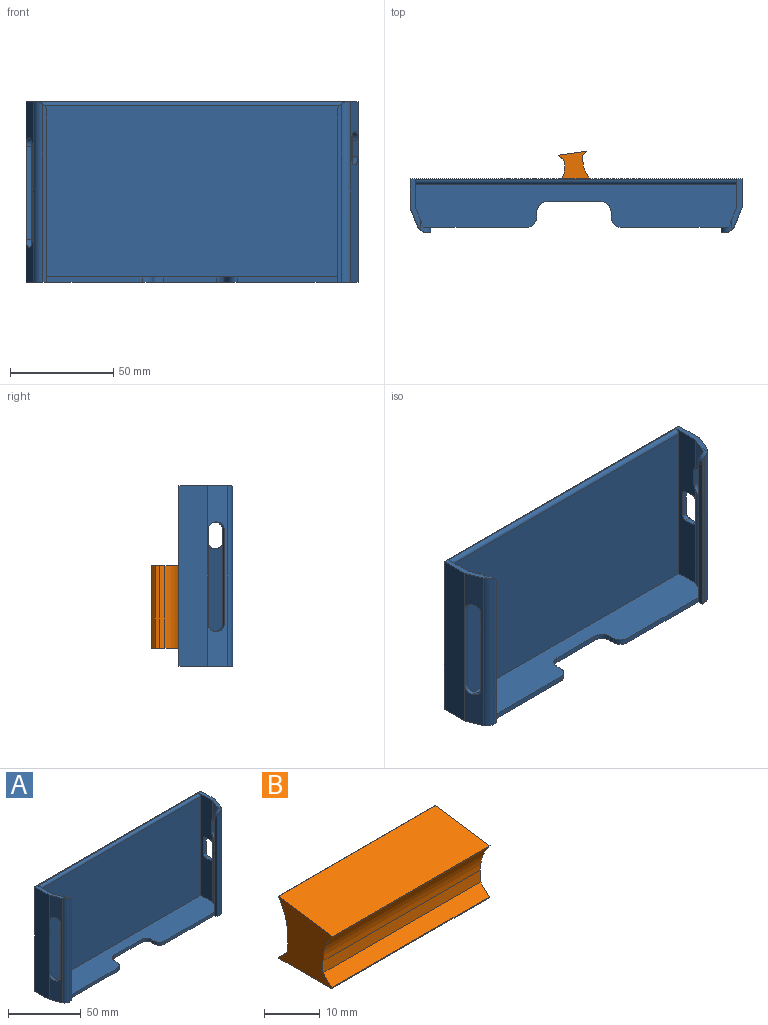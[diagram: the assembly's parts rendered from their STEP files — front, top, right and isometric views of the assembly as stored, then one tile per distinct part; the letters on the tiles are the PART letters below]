
ASSEMBLY  parts=2 mates=1
PART A: 57 faces, bbox 161x26x87.6 mm
  f0: plane 48.4x2.6mm, normal (0,-1,0), area 125.8mm2, adj f2,f3,f42,f48
  f1: plane 46.4x2.6mm, normal (0,-1,0), area 120.6mm2, adj f2,f3,f43,f52
  f2: plane 161x26mm, normal (0,0,-1), area 3307.5mm2, adj f0,f1,f6,f9,f10,f13,f14,f27
  f3: plane 155.8x20.8mm, normal (0,0,1), area 2754.5mm2, adj f0,f1,f4,f5,f8,f11,f12,f27
  f4: plane 85x13.3mm, normal (-1,0,0), area 803.1mm2, adj f3,f5,f7,f8,f15,f16,f17,f19
  f5: plane 85.03x9.53mm, normal (-0.93,0.37,0), area 750.4mm2, adj f3,f4,f7,f18,f20,f21,f22,f34
  f6: plane 87.6x9.5mm, normal (0.93,-0.37,0), area 766mm2, adj f2,f7,f14,f18,f20,f21,f22,f34
  f7: plane 161x24.93mm, normal (0,0,1), area 213.2mm2, adj f4,f5,f6,f9,f10,f11,f12,f13
  f8: plane 155.8x83mm, normal (0,-1,0), area 12931.4mm2, adj f3,f4,f12,f46
  f9: plane 161x87.6mm, normal (0,1,0), area 14103.6mm2, adj f2,f7,f13,f14
  f10: plane 87.6x9.5mm, normal (-0.93,-0.37,0), area 458.7mm2, adj f2,f7,f13,f23,f24,f25,f26,f30
  f11: plane 85.03x9.53mm, normal (0.93,0.37,0), area 467.3mm2, adj f3,f7,f12,f23,f24,f26,f30,f31
  f12: plane 85x13.3mm, normal (1,0,0), area 923.2mm2, adj f3,f7,f8,f11,f25,f31,f32,f46
  f13: plane 87.6x13.9mm, normal (-1,0,0), area 1217.6mm2, adj f2,f7,f9,f10
  f14: plane 87.6x13.9mm, normal (1,0,0), area 1071.4mm2, adj f2,f6,f7,f9,f15,f16,f17,f19
  f15: plane 4.7x2.6mm, normal (0,0,1), area 12.2mm2, adj f4,f14,f38,f39
  f16: plane 4.7x2.6mm, normal (0,0,-1), area 12.2mm2, adj f4,f14,f40,f41
  f17: plane 13.2x2.6mm, normal (0,-1,0), area 34.3mm2, adj f4,f14,f39,f40
  f18: plane 13.2x2.6mm, normal (0,1,0), area 34.3mm2, adj f5,f6,f38,f41
  f19: plane 8x2.6mm, normal (-0.37,-0.93,0), area 22.4mm2, adj f4,f14,f34,f35
  f20: plane 2.61x1.83mm, normal (0,0,1), area 2.4mm2, adj f5,f6,f34,f37
  f21: plane 2.61x1.83mm, normal (0,0,-1), area 2.4mm2, adj f5,f6,f35,f36
  f22: plane 8x2.24mm, normal (0.37,0.93,0), area 19.3mm2, adj f5,f6,f36,f37
  f23: plane 45.1x2.24mm, normal (-0.37,0.93,0), area 108.9mm2, adj f10,f11,f30,f33
  f24: plane 2.43x1.36mm, normal (0,0,-1), area 1.2mm2, adj f10,f11,f30,f31
  f25: plane 45.1x2.51mm, normal (0.37,-0.93,0), area 122.1mm2, adj f10,f12,f31,f32
  f26: plane 2.43x1.36mm, normal (0,0,1), area 1.2mm2, adj f10,f11,f32,f33
  f27: plane 2.6x2.5mm, normal (-1,0,0), area 6.5mm2, adj f2,f3,f42,f45
  f28: plane 2.6x2.5mm, normal (1,0,0), area 6.5mm2, adj f2,f3,f43,f44
  f29: plane 26x2.6mm, normal (0,-1,0), area 67.6mm2, adj f2,f3,f44,f45
  f30: cylinder r=4mm len=4.61mm, axis (0.93,0.37,0), area 15.2mm2, adj f10,f11,f23,f24
  f31: cylinder r=4mm len=4.72mm, axis (-0.93,-0.37,0), area 15.6mm2, adj f10,f11,f12,f24,f25
  f32: cylinder r=4mm len=4.72mm, axis (0.93,0.37,0), area 15.6mm2, adj f10,f11,f12,f25,f26
  f33: cylinder r=4mm len=4.61mm, axis (-0.93,-0.37,0), area 15.2mm2, adj f10,f11,f23,f26
  f34: cylinder r=4mm len=4.75mm, axis (0.93,-0.37,0), area 15.9mm2, adj f4,f5,f6,f19,f20
  f35: cylinder r=4mm len=4.75mm, axis (-0.93,0.37,0), area 15.9mm2, adj f4,f5,f6,f19,f21
  f36: cylinder r=4mm len=4.61mm, axis (-0.93,0.37,0), area 15.2mm2, adj f5,f6,f21,f22
  f37: cylinder r=4mm len=4.61mm, axis (0.93,-0.37,0), area 15.2mm2, adj f5,f6,f20,f22
  f38: cylinder r=2mm len=2.6mm, axis (1,0,0), area 8.2mm2, adj f4,f14,f15,f18
  f39: cylinder r=2mm len=2.6mm, axis (1,0,0), area 8.2mm2, adj f4,f14,f15,f17
  f40: cylinder r=2mm len=2.6mm, axis (-1,0,0), area 8.2mm2, adj f4,f14,f16,f17
  f41: cylinder r=2mm len=2.6mm, axis (-1,0,0), area 8.2mm2, adj f4,f14,f16,f18
  f42: cylinder r=5mm len=5mm, axis (0,0,1), area 20.4mm2, adj f0,f2,f3,f27
  f43: cylinder r=5mm len=5mm, axis (0,0,-1), area 20.4mm2, adj f1,f2,f3,f28
  f44: cylinder r=5mm len=5mm, axis (0,0,1), area 20.4mm2, adj f2,f3,f28,f29
  f45: cylinder r=5mm len=5mm, axis (0,0,-1), area 20.4mm2, adj f2,f3,f27,f29
  f46: cylinder r=2mm len=155.8mm, axis (1,0,0), area 489.5mm2, adj f4,f7,f8,f12
  f47: plane 84.83x3.7mm, normal (0,1,0), area 309.2mm2, adj f3,f5,f48,f50
  f48: plane 82.6x2.6mm, normal (-1,0,0), area 214.8mm2, adj f0,f2,f47,f49,f50
  f49: plane 86.53x1.91mm, normal (0,-1,0), area 163.3mm2, adj f2,f48,f50,f51
  f50: cylinder r=5mm len=5.85mm, axis (0,-1,0), area 21.5mm2, adj f5,f7,f47,f48,f49,f51
  f51: cylinder r=5mm len=87.6mm, axis (0,0,-1), area 467.7mm2, adj f2,f6,f7,f49,f50
  f52: plane 82.6x2.6mm, normal (1,0,0), area 214.8mm2, adj f1,f2,f53,f54,f55
  f53: plane 86.53x1.91mm, normal (0,-1,0), area 163.3mm2, adj f2,f52,f55,f56
  f54: plane 84.83x3.7mm, normal (0,1,0), area 309.2mm2, adj f3,f11,f52,f55
  f55: cylinder r=5mm len=5.85mm, axis (0,1,0), area 21.5mm2, adj f7,f11,f52,f53,f54,f56
  f56: cylinder r=5mm len=87.6mm, axis (0,0,1), area 467.7mm2, adj f2,f7,f10,f53,f55
PART B: 13 faces, bbox 40x13.9x13.6 mm
  f0: plane 40x2.62mm, normal (0,-1,0), area 104.7mm2, adj f3,f5,f7,f12
  f1: plane 40x3.91mm, normal (0,1,0), area 156.5mm2, adj f3,f5,f8,f11
  f2: plane 40x0.2mm, normal (0,1,0), area 8mm2, adj f3,f5,f6,f8
  f3: plane 13.86x13.55mm, normal (-1,0,0), area 129.3mm2, adj f0,f1,f2,f4,f6,f7,f8,f9
  f4: plane 40x0.2mm, normal (0,-1,0), area 8mm2, adj f3,f5,f6,f7
  f5: plane 13.86x13.55mm, normal (1,0,0), area 129.3mm2, adj f0,f1,f2,f4,f6,f7,f8,f9
  f6: plane 40x13.4mm, normal (0,0,-1), area 536mm2, adj f2,f3,f4,f5
  f7: plane 40x2.2mm, normal (0,-0.71,0.71), area 124.5mm2, adj f0,f3,f4,f5
  f8: plane 40x2.2mm, normal (0,0.71,0.71), area 124.5mm2, adj f1,f2,f3,f5
  f9: plane 40x13.86mm, normal (0,-0.14,0.99), area 560mm2, adj f3,f5,f10,f12
  f10: plane 40x0.05mm, normal (0,0.8,-0.6), area 2.6mm2, adj f3,f5,f9,f11
  f11: cylinder r=12mm len=40mm, axis (-1,0,0), area 308.1mm2, adj f1,f3,f5,f10
  f12: cylinder r=10mm len=40mm, axis (-1,0,0), area 284.7mm2, adj f0,f3,f5,f9
PLACE A at identity
PLACE B rot(axis=(0.55,0.63,-0.55),115.4deg) t=(-8.43,11.46,3.7)mm
MATE fastened B.f9 <-> A.f9  axis (0,-1,0) through (0,0,-16.3)mm
